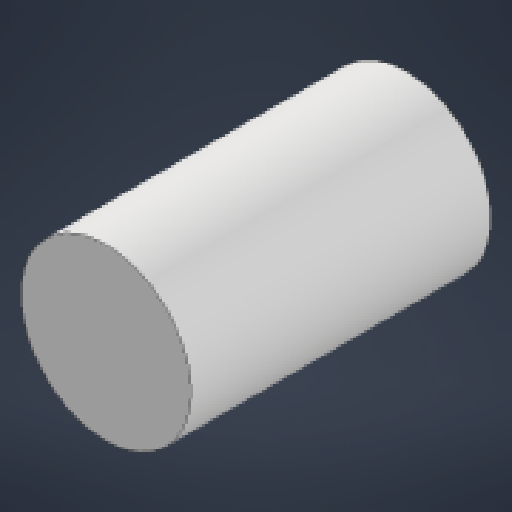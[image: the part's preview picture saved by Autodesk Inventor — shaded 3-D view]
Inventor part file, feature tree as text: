
AUTODESK INVENTOR PART (.ipt)
format: ipt  version: 2024.1 (Build 281209000, 209)  size: 263,680 bytes
history: native  units: in
note: dims shown in document units (in); Inventor stores cm internally (conversion verified against a paired STEP export)
features: extrude x5, sketch x2, plane x2, chamfer x2, other x2, mirror x1, reference x1
ambient origin geometry x8: Origin, YZ Plane, XZ Plane, XY Plane, X Axis, Y Axis, Z Axis, Center Point
bodies: Solid1 (feature_tree)
feature tree (15):
  sketch  "Sketch1"  dims[d0=0.219in d1=0.219in]
  extrude  "Extrusion1"  Depth=0.219in
  extrude  "Extrusion2"  Depth=0.219in
  extrude  "Extrusion3"  Depth=2.6496in TaperAngle=0.0deg
  plane  "Work Plane1"
  mirror  "Mirror1"
  chamfer  "Chamfer1"  Distance=0.315in
  plane  "Work Plane3"
  sketch  "Sketch3"  dims[d2=0.219in d3=0.219in d4=2.6496in d5=0.0in d6=0.315in d7=0.0in d8=0.75in d9=0.0in d10=0.025in d11=0.125in d12=45.0deg d14=11.2018in d15=0.5in d16=0.5in d17=0.3in d18=0.3in d19=0.0in d20=0.0in d21=0.2in d22=0.0in d23=0.15in d24=0.125in d25=45.0deg]
  extrude  "Extrusion4"  Depth=0.75in TaperAngle=0.0deg
  extrude  "Extrusion5"  Depth=0.025in TaperAngle=45.0deg
  chamfer  "Chamfer2"  Distance=11.2018in
  reference  "Reference1"
  other  "Assembly1"
  other  "MainArm:2"
